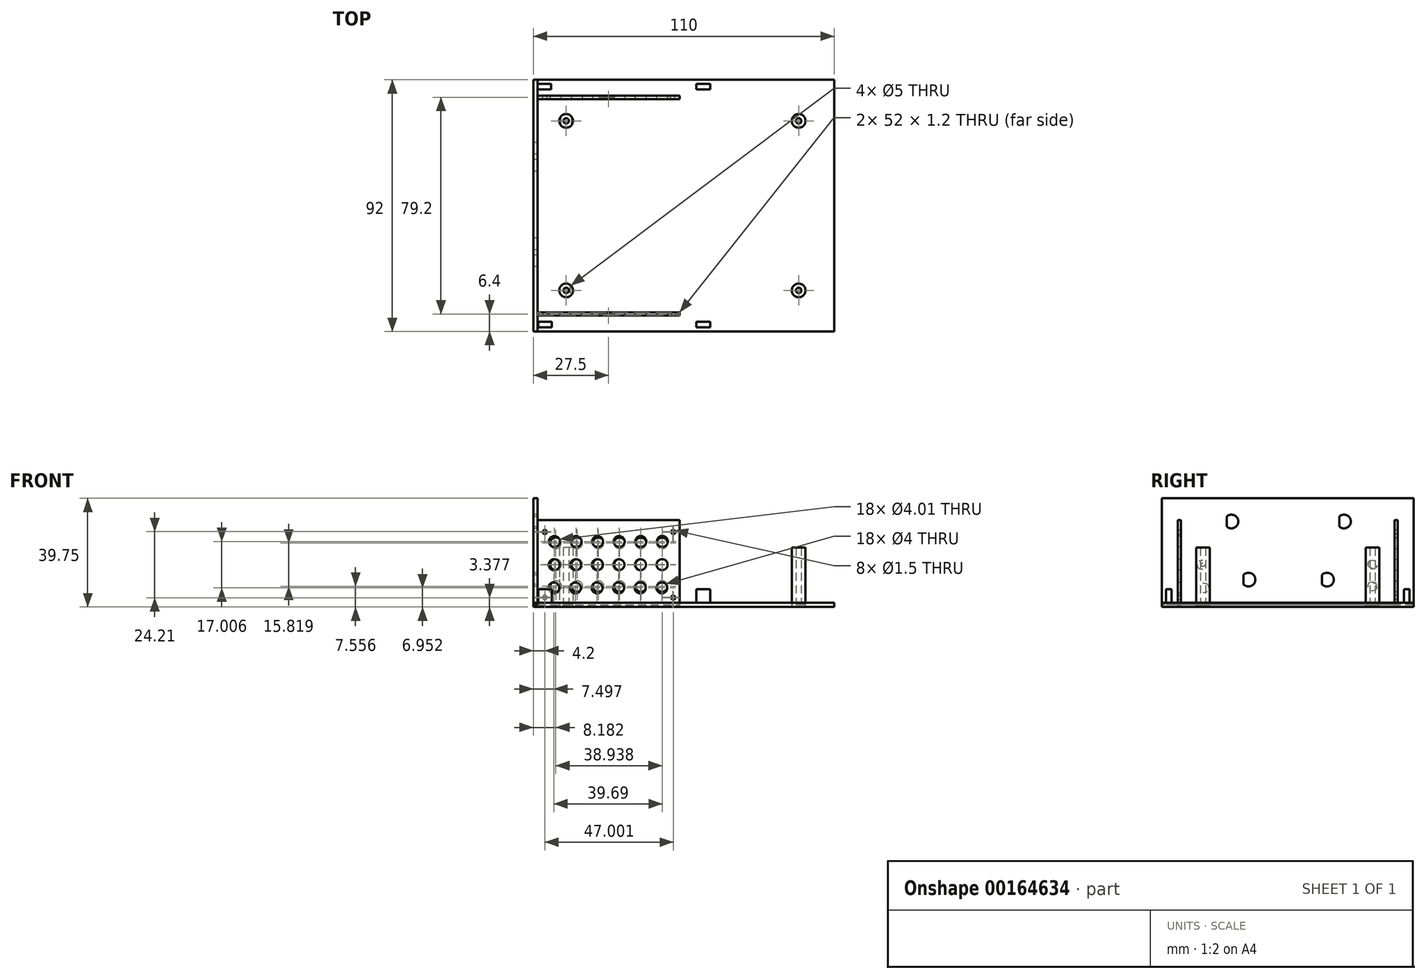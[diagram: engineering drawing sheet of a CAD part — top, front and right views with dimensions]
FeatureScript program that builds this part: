
annotation { "Feature Type Name" : "Feature", "Feature Type Description" : "" }
export const myFeature = defineFeature(function(context is Context, id is Id, definition is map)
    precondition{}
    {
        {
            var Q0;
            Q0=qCreatedBy(makeId("Top.planeOp"),FACE);
            var sketch = newSketch(context, id + "F0", { "sketchPlane" : qUnion([Q0])});
            skLineSegment(sketch, "E0.bottom", {"start": v(-55, 46) * mm, "end": v(55, 46) * mm});
            skLineSegment(sketch, "E0.top", {"start": v(-55, -46) * mm, "end": v(55, -46) * mm});
            skLineSegment(sketch, "E0.left", {"start": v(-55, 46) * mm, "end": v(-55, -46) * mm});
            skLineSegment(sketch, "E0.right", {"start": v(55, 46) * mm, "end": v(55, -46) * mm});
            skPoint(sketch, "E0.middle", {"position": v(0, 0) * mm});
            skLineSegment(sketch, "E1.0", {"start": v(-53.5, 46) * mm, "end": v(-53.5, -46) * mm});
            skCircle(sketch, "E2", {"center": v(42, 31) * mm, "radius": 2.5 * mm});
            skCircle(sketch, "E3", {"center": v(-43, 31) * mm, "radius": 2.5 * mm});
            skCircle(sketch, "E4", {"center": v(-43, -31) * mm, "radius": 2.5 * mm});
            skCircle(sketch, "E5", {"center": v(42, -31) * mm, "radius": 2.5 * mm});
            skLineSegment(sketch, "E6.bottom", {"start": v(-53.5, 40.2) * mm, "end": v(-1.5, 40.2) * mm});
            skLineSegment(sketch, "E6.top", {"start": v(-53.5, 39) * mm, "end": v(-1.5, 39) * mm});
            skLineSegment(sketch, "E6.left", {"start": v(-53.5, 40.2) * mm, "end": v(-53.5, 39) * mm});
            skLineSegment(sketch, "E6.right", {"start": v(-1.5, 40.2) * mm, "end": v(-1.5, 39) * mm});
            skLineSegment(sketch, "E7.MirrorCS", {"start": v(-53.5, -39) * mm, "end": v(-1.5, -39) * mm});
            skLineSegment(sketch, "E8.MirrorCS", {"start": v(-53.5, -40.2) * mm, "end": v(-1.5, -40.2) * mm});
            skLineSegment(sketch, "E9.MirrorCS", {"start": v(-1.5, -40.2) * mm, "end": v(-1.5, -39) * mm});
            skCircle(sketch, "E10.0", {"center": v(-43, -31) * mm, "radius": 1 * mm});
            skCircle(sketch, "E11.0", {"center": v(42, -31) * mm, "radius": 1 * mm});
            skCircle(sketch, "E12.0", {"center": v(42, 31) * mm, "radius": 1 * mm});
            skCircle(sketch, "E13.0", {"center": v(-43, 31) * mm, "radius": 1 * mm});
            skSolve(sketch);
        }
        {
            var Q0;
            Q0=makeQuery(id+"F0.imprint","IMPRINT",FACE,{"disambiguationData":[TD([[makeQuery(id+"F0.imprint","IMPRINT",EDGE,{"derivedFrom":sQuery(id+"F0.wireOp",EDGE,"E3")}),1.0]])]});
            var Q1;
            Q1=makeQuery(id+"F0.imprint","IMPRINT",FACE,{"disambiguationData":[TD([[makeQuery(id+"F0.imprint","IMPRINT",EDGE,{"derivedFrom":sQuery(id+"F0.wireOp",EDGE,"E4")}),1.0]])]});
            var Q2;
            Q2=makeQuery(id+"F0.imprint","IMPRINT",FACE,{"disambiguationData":[TD([[makeQuery(id+"F0.imprint","IMPRINT",EDGE,{"derivedFrom":sQuery(id+"F0.wireOp",EDGE,"E5")}),1.0]])]});
            var Q3;
            Q3=makeQuery(id+"F0.imprint","IMPRINT",FACE,{"disambiguationData":[TD([[makeQuery(id+"F0.imprint","IMPRINT",EDGE,{"derivedFrom":sQuery(id+"F0.wireOp",EDGE,"E2")}),1.0]])]});
            extrude(context, id + "F1", {"entities" : qUnion([Q0, Q1, Q2, Q3]), "depth" : 21 * mm});
        }
        {
            var Q0;
            {var subQ4=sQuery(id+"F0.wireOp",EDGE,"E0.left");Q0=makeQuery(id+"F0.imprint","IMPRINT",FACE,{"disambiguationData":[TD([[makeQuery(id+"F0.imprint","IMPRINT",EDGE,{"derivedFrom":subQ4}),1.0]])]});}
            extrude(context, id + "F2", {"entities" : qUnion([Q0]), "depth" : 39 * mm});
        }
        {
            var Q0;
            Q0=makeQuery(id+"F0.imprint","IMPRINT",FACE,{"disambiguationData":[TD([[makeQuery(id+"F0.imprint","IMPRINT",EDGE,{"derivedFrom":sQuery(id+"F0.wireOp",EDGE,"E6.bottom")}),-1.0]])]});
            var Q1;
            {var subQ0=sQuery(id+"F0.wireOp",EDGE,"E7.MirrorCS");Q1=makeQuery(id+"F0.imprint","IMPRINT",FACE,{"disambiguationData":[TD([[makeQuery(id+"F0.imprint","IMPRINT",EDGE,{"derivedFrom":subQ0}),-1.0]])]});}
            var Q2;
            Q2 = qSketchRegion(id + "F4", true);
            extrude(context, id + "F3", {"entities" : qUnion([Q0, Q1, Q2]), "operationType" : NewBodyOperationType.ADD, "depth" : 31 * mm});
        }
        {
            var Q0;
            Q0=makeQuery(id+"F3.opExtrude","SWEPT_FACE",FACE,{"disambiguationData":[OSD([sQuery(id+"F0.wireOp",EDGE,"E6.bottom")])]});
            var sketch = newSketch(context, id + "F4", { "sketchPlane" : qUnion([Q0])});
            skCircle(sketch, "E14", {"center": v(4, 26.84) * mm, "radius": 0.75 * mm});
            skCircle(sketch, "E15", {"center": v(50.8, 26.84) * mm, "radius": 0.75 * mm});
            skCircle(sketch, "E16", {"center": v(50.8, 2.84) * mm, "radius": 0.75 * mm});
            skCircle(sketch, "E17", {"center": v(4, 2.84) * mm, "radius": 0.75 * mm});
            skCircle(sketch, "E18", {"center": v(7.92, 22.6) * mm, "radius": 2 * mm});
            skCircle(sketch, "E19.0.1.0", {"center": v(7.9, 14.7) * mm, "radius": 2 * mm});
            skCircle(sketch, "E19.0.2.0", {"center": v(7.88, 6.8) * mm, "radius": 2 * mm});
            skCircle(sketch, "E19.1.0.0", {"center": v(15.7, 22.6) * mm, "radius": 2 * mm});
            skCircle(sketch, "E19.1.1.0", {"center": v(15.68, 14.7) * mm, "radius": 2 * mm});
            skCircle(sketch, "E19.1.2.0", {"center": v(15.66, 6.81) * mm, "radius": 2 * mm});
            skCircle(sketch, "E19.2.0.0", {"center": v(23.48, 22.6) * mm, "radius": 2 * mm});
            skCircle(sketch, "E19.2.1.0", {"center": v(23.46, 14.71) * mm, "radius": 2 * mm});
            skCircle(sketch, "E19.2.2.0", {"center": v(23.44, 6.82) * mm, "radius": 2 * mm});
            skCircle(sketch, "E19.3.0.0", {"center": v(31.26, 22.61) * mm, "radius": 2 * mm});
            skCircle(sketch, "E19.3.1.0", {"center": v(31.24, 14.72) * mm, "radius": 2 * mm});
            skCircle(sketch, "E19.3.2.0", {"center": v(31.22, 6.83) * mm, "radius": 2 * mm});
            skCircle(sketch, "E19.4.0.0", {"center": v(39.04, 22.62) * mm, "radius": 2 * mm});
            skCircle(sketch, "E19.4.1.0", {"center": v(39.02, 14.73) * mm, "radius": 2 * mm});
            skCircle(sketch, "E19.4.2.0", {"center": v(39, 6.83) * mm, "radius": 2 * mm});
            skCircle(sketch, "E19.5.0.0", {"center": v(46.82, 22.63) * mm, "radius": 2 * mm});
            skCircle(sketch, "E19.5.1.0", {"center": v(46.8, 14.73) * mm, "radius": 2 * mm});
            skCircle(sketch, "E19.5.2.0", {"center": v(46.78, 6.84) * mm, "radius": 2 * mm});
            skLineSegment(sketch, "E19.direction1", {"start": v(7.92, 22.6) * mm, "end": v(15.7, 22.6) * mm, "construction": true});
            skLineSegment(sketch, "E19.direction2", {"start": v(7.92, 22.6) * mm, "end": v(7.9, 14.7) * mm, "construction": true});
            skSolve(sketch);
        }
        {
            var Q0;
            Q0 = qSketchRegion(id + "F4", true);
            extrude(context, id + "F5", {"entities" : qUnion([Q0]), "operationType" : NewBodyOperationType.REMOVE, "oppositeDirection" : true, "depth" : 25 * mm});
        }
        {
            var Q0;
            Q0=makeQuery(id+"F3.opExtrude","SWEPT_FACE",FACE,{"disambiguationData":[OSD([sQuery(id+"F0.wireOp",EDGE,"E8.MirrorCS")])]});
            var sketch = newSketch(context, id + "F6", { "sketchPlane" : qUnion([Q0])});
            skCircle(sketch, "E20", {"center": v(-50.8, 26.63) * mm, "radius": 0.75 * mm});
            skCircle(sketch, "E21", {"center": v(-3.8, 26.63) * mm, "radius": 0.75 * mm});
            skCircle(sketch, "E22", {"center": v(-3.8, 2.63) * mm, "radius": 0.75 * mm});
            skCircle(sketch, "E23", {"center": v(-50.8, 2.63) * mm, "radius": 0.75 * mm});
            skCircle(sketch, "E24", {"center": v(-47.3, 23.2) * mm, "radius": 2 * mm});
            skCircle(sketch, "E25.0.1.0", {"center": v(-47.4, 14.7) * mm, "radius": 2 * mm});
            skCircle(sketch, "E25.0.2.0", {"center": v(-47.5, 6.2) * mm, "radius": 2 * mm});
            skCircle(sketch, "E25.1.0.0", {"center": v(-39.4, 23.2) * mm, "radius": 2 * mm});
            skCircle(sketch, "E25.1.1.0", {"center": v(-39.5, 14.7) * mm, "radius": 2 * mm});
            skCircle(sketch, "E25.1.2.0", {"center": v(-39.6, 6.2) * mm, "radius": 2 * mm});
            skCircle(sketch, "E25.2.0.0", {"center": v(-31.5, 23.2) * mm, "radius": 2 * mm});
            skCircle(sketch, "E25.2.1.0", {"center": v(-31.6, 14.7) * mm, "radius": 2 * mm});
            skCircle(sketch, "E25.2.2.0", {"center": v(-31.7, 6.2) * mm, "radius": 2 * mm});
            skCircle(sketch, "E25.3.0.0", {"center": v(-23.6, 23.2) * mm, "radius": 2 * mm});
            skCircle(sketch, "E25.3.1.0", {"center": v(-23.7, 14.7) * mm, "radius": 2 * mm});
            skCircle(sketch, "E25.3.2.0", {"center": v(-23.81, 6.2) * mm, "radius": 2 * mm});
            skCircle(sketch, "E25.4.0.0", {"center": v(-15.7, 23.2) * mm, "radius": 2 * mm});
            skCircle(sketch, "E25.4.1.0", {"center": v(-15.81, 14.7) * mm, "radius": 2 * mm});
            skCircle(sketch, "E25.4.2.0", {"center": v(-15.92, 6.21) * mm, "radius": 2 * mm});
            skCircle(sketch, "E25.5.0.0", {"center": v(-7.81, 23.2) * mm, "radius": 2 * mm});
            skCircle(sketch, "E25.5.1.0", {"center": v(-7.92, 14.71) * mm, "radius": 2 * mm});
            skCircle(sketch, "E25.5.2.0", {"center": v(-8.02, 6.21) * mm, "radius": 2 * mm});
            skLineSegment(sketch, "E25.direction1", {"start": v(-47.3, 23.2) * mm, "end": v(-39.4, 23.2) * mm, "construction": true});
            skLineSegment(sketch, "E25.direction2", {"start": v(-47.3, 23.2) * mm, "end": v(-47.4, 14.7) * mm, "construction": true});
            skSolve(sketch);
        }
        {
            var Q0;
            Q0 = qSketchRegion(id + "F6", true);
            extrude(context, id + "F7", {"entities" : qUnion([Q0]), "operationType" : NewBodyOperationType.REMOVE, "oppositeDirection" : true, "depth" : 25 * mm});
        }
        {
            var Q0;
            Q0 = qSketchRegion(id + "F0", true);
            extrude(context, id + "F8", {"entities" : qUnion([Q0]), "endBound" : BoundingType.SYMMETRIC, "oppositeDirection" : true, "depth" : 1.5 * mm});
        }
        {
            var Q0;
            Q0=makeQuery(id+"F2.opExtrude","SWEPT_FACE",FACE,{"disambiguationData":[OSD([sQuery(id+"F0.wireOp",EDGE,"E0.left")])]});
            var sketch = newSketch(context, id + "F9", { "sketchPlane" : qUnion([Q0])});
            skLineSegment(sketch, "E26.0", {"start": v(-51, -5) * mm, "end": v(51, -5) * mm});
            skLineSegment(sketch, "E26.1", {"start": v(-51, 44) * mm, "end": v(-51, -5) * mm});
            skLineSegment(sketch, "E26.2", {"start": v(51, 44) * mm, "end": v(-51, 44) * mm});
            skLineSegment(sketch, "E26.3", {"start": v(51, -5) * mm, "end": v(51, 44) * mm});
            skPoint(sketch, "E27.middle", {"position": v(0, 9.25) * mm});
            skPoint(sketch, "E28.middle", {"position": v(0, 20.3) * mm});
            skArc(sketch, "E29", {"start": v(-18.87, 32.33) * mm, "mid": v(-23.08, 30.5) * mm, "end": v(-18.87, 28.67) * mm});
            skArc(sketch, "E30", {"start": v(22.27, 32.34) * mm, "mid": v(18.08, 30.5) * mm, "end": v(22.27, 28.66) * mm});
            skLineSegment(sketch, "E31", {"start": v(-18.87, 32.33) * mm, "end": v(-18.87, 28.67) * mm});
            skLineSegment(sketch, "E32", {"start": v(22.27, 32.34) * mm, "end": v(22.27, 28.66) * mm});
            skPoint(sketch, "E33.startSnap0", {"position": v(-38.92, 9.25) * mm});
            skArc(sketch, "E34", {"start": v(-12.5, 10.94) * mm, "mid": v(-16.84, 9.25) * mm, "end": v(-12.5, 7.56) * mm});
            skArc(sketch, "E35", {"start": v(16.19, 10.93) * mm, "mid": v(11.84, 9.25) * mm, "end": v(16.19, 7.57) * mm});
            skLineSegment(sketch, "E36", {"start": v(-12.5, 10.94) * mm, "end": v(-12.5, 7.56) * mm});
            skLineSegment(sketch, "E37", {"start": v(16.19, 10.93) * mm, "end": v(16.19, 7.57) * mm});
            skText(sketch, "E38", { "text": "M-CHAIN 0", "fontName": "OpenSans-Bold.ttf"});
            skText(sketch, "E39", { "text": "M-CHAIN1", "fontName": "OpenSans-Bold.ttf"});
            skText(sketch, "E40", { "text": "LTE-1", "fontName": "OpenSans-Bold.ttf"});
            skText(sketch, "E41", { "text": "LTE-2", "fontName": "OpenSans-Bold.ttf"});
            const initialGuessF9  = {"E38": [-0.03288, 0.02209, 1, 0, 0.00337], "E39": [0.00953, 0.02255, 1, 0, 0.00306], "E40": [-0.01964, 0.0028, 1, 0, 0.00299], "E41": [0.00846, 0.0028, 1, 0, 0.00314]};
            skSetInitialGuess(sketch, initialGuessF9);
            skSolve(sketch);
        }
        {
            var Q0;
            Q0=makeQuery(id+"F9.imprint","IMPRINT",FACE,{"disambiguationData":[TD([[makeQuery(id+"F9.imprint","IMPRINT",EDGE,{"derivedFrom":sQuery(id+"F9.wireOp",EDGE,"E29")}),1.0]])]});
            var Q1;
            Q1=makeQuery(id+"F9.imprint","IMPRINT",FACE,{"disambiguationData":[TD([[makeQuery(id+"F9.imprint","IMPRINT",EDGE,{"derivedFrom":sQuery(id+"F9.wireOp",EDGE,"E30")}),1.0]])]});
            var Q2;
            Q2=makeQuery(id+"F9.imprint","IMPRINT",FACE,{"disambiguationData":[TD([[makeQuery(id+"F9.imprint","IMPRINT",EDGE,{"derivedFrom":sQuery(id+"F9.wireOp",EDGE,"E34")}),1.0]])]});
            var Q3;
            Q3=makeQuery(id+"F9.imprint","IMPRINT",FACE,{"disambiguationData":[TD([[makeQuery(id+"F9.imprint","IMPRINT",EDGE,{"derivedFrom":sQuery(id+"F9.wireOp",EDGE,"E35")}),1.0]])]});
            extrude(context, id + "F10", {"entities" : qUnion([Q0, Q1, Q2, Q3]), "operationType" : NewBodyOperationType.REMOVE, "oppositeDirection" : true, "depth" : 25 * mm});
        }
        {
            var Q0;
            Q0=makeQuery(id+"F8.opExtrude","CAP_FACE",FACE,{"disambiguationData":[OSD([sQuery(id+"F0.wireOp",EDGE,"E0.bottom"),sQuery(id+"F0.wireOp",EDGE,"E0.top"),sQuery(id+"F0.wireOp",EDGE,"E0.left"),sQuery(id+"F0.wireOp",EDGE,"E0.right"),sQuery(id+"F0.wireOp",EDGE,"E1.0"),sQuery(id+"F0.wireOp",EDGE,"E2"),sQuery(id+"F0.wireOp",EDGE,"E3"),sQuery(id+"F0.wireOp",EDGE,"E4"),sQuery(id+"F0.wireOp",EDGE,"E5"),sQuery(id+"F0.wireOp",EDGE,"E6.bottom"),sQuery(id+"F0.wireOp",EDGE,"E6.top"),sQuery(id+"F0.wireOp",EDGE,"E6.left"),sQuery(id+"F0.wireOp",EDGE,"E6.right"),sQuery(id+"F0.wireOp",EDGE,"E7.MirrorCS"),sQuery(id+"F0.wireOp",EDGE,"E8.MirrorCS"),sQuery(id+"F0.wireOp",EDGE,"E9.MirrorCS")])],"isStart":true});
            var sketch = newSketch(context, id + "F11", { "sketchPlane" : qUnion([Q0])});
            skLineSegment(sketch, "E42.0", {"start": v(53.5, 46) * mm, "end": v(53.5, -46) * mm});
            skLineSegment(sketch, "E43.bottom", {"start": v(4.63, 44.5) * mm, "end": v(9.63, 44.5) * mm});
            skLineSegment(sketch, "E43.top", {"start": v(4.63, 42.5) * mm, "end": v(9.63, 42.5) * mm});
            skLineSegment(sketch, "E43.left", {"start": v(4.63, 44.5) * mm, "end": v(4.63, 42.5) * mm});
            skLineSegment(sketch, "E43.right", {"start": v(9.63, 44.5) * mm, "end": v(9.63, 42.5) * mm});
            skLineSegment(sketch, "E44.bottom", {"start": v(4.63, -42.5) * mm, "end": v(9.63, -42.5) * mm});
            skLineSegment(sketch, "E44.top", {"start": v(4.63, -44.5) * mm, "end": v(9.63, -44.5) * mm});
            skLineSegment(sketch, "E44.left", {"start": v(4.63, -42.5) * mm, "end": v(4.63, -44.5) * mm});
            skLineSegment(sketch, "E44.right", {"start": v(9.63, -42.5) * mm, "end": v(9.63, -44.5) * mm});
            skLineSegment(sketch, "E45.bottom", {"start": v(-53.24, -42.5) * mm, "end": v(-48.24, -42.5) * mm});
            skLineSegment(sketch, "E45.top", {"start": v(-53.24, -44.5) * mm, "end": v(-48.24, -44.5) * mm});
            skLineSegment(sketch, "E45.left", {"start": v(-53.24, -42.5) * mm, "end": v(-53.24, -44.5) * mm});
            skLineSegment(sketch, "E45.right", {"start": v(-48.24, -42.5) * mm, "end": v(-48.24, -44.5) * mm});
            skLineSegment(sketch, "E46.bottom", {"start": v(-53.5, 44.5) * mm, "end": v(-48.5, 44.5) * mm});
            skLineSegment(sketch, "E46.top", {"start": v(-53.5, 42.5) * mm, "end": v(-48.5, 42.5) * mm});
            skLineSegment(sketch, "E46.left", {"start": v(-53.5, 44.5) * mm, "end": v(-53.5, 42.5) * mm});
            skLineSegment(sketch, "E46.right", {"start": v(-48.5, 44.5) * mm, "end": v(-48.5, 42.5) * mm});
            skLineSegment(sketch, "E47.left", {"start": v(-1.5, 40.2) * mm, "end": v(-1.5, 39) * mm});
            skLineSegment(sketch, "E48.left", {"start": v(-1.5, -39) * mm, "end": v(-1.5, -40.22) * mm});
            skSolve(sketch);
        }
        {
            var Q0;
            Q0=makeQuery(id+"F11.imprint","IMPRINT",FACE,{"disambiguationData":[TD([[makeQuery(id+"F11.imprint","IMPRINT",EDGE,{"derivedFrom":sQuery(id+"F11.wireOp",EDGE,"E44.bottom")}),-1.0]])]});
            var Q1;
            Q1=makeQuery(id+"F11.imprint","IMPRINT",FACE,{"disambiguationData":[TD([[makeQuery(id+"F11.imprint","IMPRINT",EDGE,{"derivedFrom":sQuery(id+"F11.wireOp",EDGE,"E43.bottom")}),-1.0]])]});
            var Q2;
            Q2=makeQuery(id+"F11.imprint","IMPRINT",FACE,{"disambiguationData":[TD([[makeQuery(id+"F11.imprint","IMPRINT",EDGE,{"derivedFrom":sQuery(id+"F11.wireOp",EDGE,"E46.bottom")}),-1.0]])]});
            var Q3;
            Q3=makeQuery(id+"F11.imprint","IMPRINT",FACE,{"disambiguationData":[TD([[makeQuery(id+"F11.imprint","IMPRINT",EDGE,{"derivedFrom":sQuery(id+"F11.wireOp",EDGE,"E45.bottom")}),-1.0]])]});
            extrude(context, id + "F12", {"entities" : qUnion([Q0, Q1, Q2, Q3]), "depth" : 5 * mm});
        }
    });
